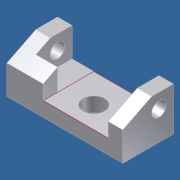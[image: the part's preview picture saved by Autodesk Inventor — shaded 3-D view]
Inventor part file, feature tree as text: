
AUTODESK INVENTOR PART (.ipt)
format: ipt  version: unknown  size: 229,888 bytes
history: native  units: in
note: dims shown in document units (in); Inventor stores cm internally (conversion verified against a paired STEP export)
features: sketch x7, extrude x3, hole x3
ambient origin geometry x8: Origin, YZ Plane, XZ Plane, XY Plane, X Axis, Y Axis, Z Axis, Center Point
bodies: Solid1 (feature_tree)
feature tree (13):
  extrude  "Extrusion1"  Depth=1.0in
  extrude  "Extrusion2"  Depth=2.5in
  sketch  "Sketch3"  dims[d4=4.5in d5=3.0in]
  hole  "Hole1"  [1 undecoded]
  sketch  "Sketch5"  dims[d9=1.0in d10=2.0in]
  extrude  "Extrusion3"  Depth=1.5in
  hole  "Hole2"  [1 undecoded]
  hole  "Hole3"  [1 undecoded]
  sketch  "Sketch1"  dims[d0=8.0in d1=1.0in]
  sketch  "Sketch2"  dims[d2=2.0in d3=2.5in]
  sketch  "Sketch4"  dims[d6=3.5in d7=0.0in d8=1.5in]
  sketch  "Sketch6"  dims[d11=3.5in d12=0.0in d13=1.5in]
  sketch  "Sketch7"  dims[d14=3.5in d15=1.0in d16=0.75in d17=0.375in d18=0.25in d19=0.5635in d20=1.0in d21=0.8108in d22=1.0in d23=1.0in d24=2.5in d25=2.0in d26=0.0in d27=1.0in d28=1.0in d29=1.0in d30=0.75in d31=0.375in d32=0.25in d33=0.5635in d34=1.0in d35=0.8108in d36=1.5in d37=0.75in d38=0.375in d39=0.25in d40=0.5635in d41=1.0in d42=0.8108in]
note: 3 required parameter values undecoded (feature->parameter linkage not recoverable at this tier; creation-order binding heuristic only, values carry confidence <= 0.55)
